# Revit family: 05f18a67-5783-43af-b561-dbd2828028a7
name_source: partatom
category: Plumbing Fixtures
revit_build: Autodesk Revit 2016 (Build: 20161004_0715(x64)
units: mm (PartAtom-declared; Revit-internal decimal feet)

## family parameters
Cut with Voids When Loaded = No
Host = Face
OmniClass Number = 23.45.05.21.11.11
OmniClass Title = Water Operated Water Closets
Part Type = Normal
Room Calculation Point = No
Round Connector Dimension = Use Radius
Shared = No

## types (1)
- Vitreous_China-0-White
    Assembly Code = D2010110
    CW Connection = Yes
    CWFU = 0
    Cold Water Connection = Cold Water Connector In
    Cold Water Diameter = 1"
    Cold Water Radius = 0"
    Default Elevation = 0' - 0"
    Description = Cavata, The Complete Solution Toilet
    Finish = Vitreous China-Kohler-0-White
    Flush Handle = Metal-Kohler-CP-Polished Chrome
    HW Connection = No
    Height = 2' - 6 1/2"
    Length = 2' - 5 3/4"
    Manufacturer = Kohler
    Model = K-45989-0
    Product Documentation Link = http://www.us.kohler.com
    Product Page URL = http://www.us.kohler.com
    Sanitary Connection = Sanitary Connector Out
    Sanitary Diameter = 3"
    Sanitary Radius = 2"
    Type Image = <None>
    URL = http://www.us.kohler.com
    Vent Connection = No
    WFU = 0
    Waste Connection = Yes
    Width = 1' - 7 3/4"

## geometry (parser evidence)
native form markers: Blend x22, Sweep x8
no freeform markers — native parametric forms only
